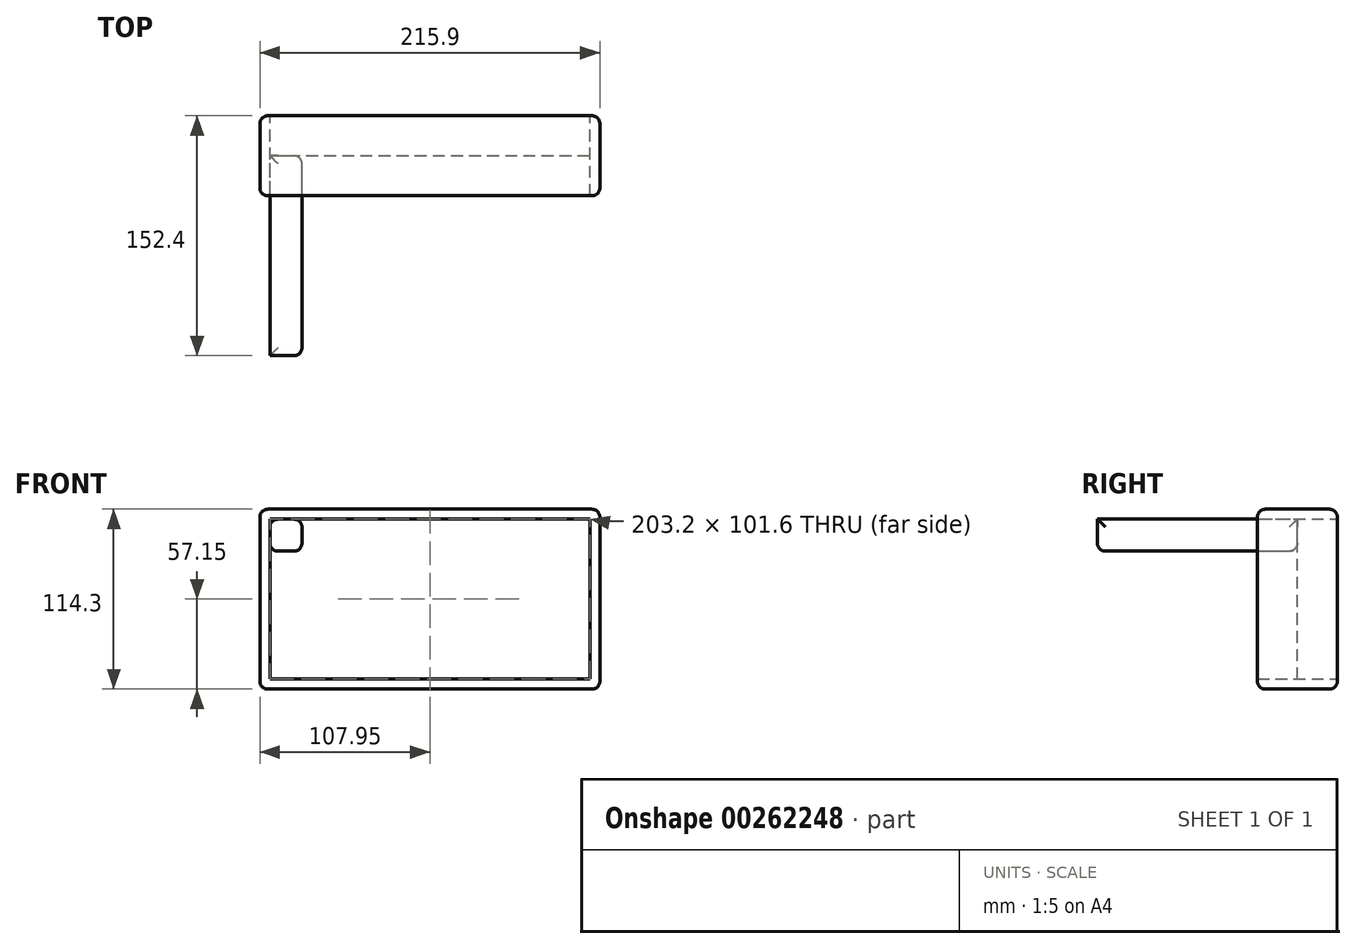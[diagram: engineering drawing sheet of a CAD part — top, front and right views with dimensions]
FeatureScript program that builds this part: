
annotation { "Feature Type Name" : "Feature", "Feature Type Description" : "" }
export const myFeature = defineFeature(function(context is Context, id is Id, definition is map)
    precondition{}
    {
        {
            var Q0;
            Q0=qCreatedBy(makeId("Front.planeOp"),FACE);
            var sketch = newSketch(context, id + "F0", { "sketchPlane" : qUnion([Q0])});
            skLineSegment(sketch, "E0.bottom", {"start": v(-101.6, -50.8) * mm, "end": v(101.6, -50.8) * mm});
            skLineSegment(sketch, "E0.top", {"start": v(-101.6, 50.8) * mm, "end": v(101.6, 50.8) * mm});
            skLineSegment(sketch, "E0.left", {"start": v(-101.6, -50.8) * mm, "end": v(-101.6, 50.8) * mm});
            skLineSegment(sketch, "E0.right", {"start": v(101.6, -50.8) * mm, "end": v(101.6, 50.8) * mm});
            skPoint(sketch, "E0.middle", {"position": v(0, 0) * mm});
            skLineSegment(sketch, "E1.bottom", {"start": v(-101.6, 30.48) * mm, "end": v(-81.28, 30.48) * mm});
            skLineSegment(sketch, "E1.top", {"start": v(-101.6, 50.8) * mm, "end": v(-81.28, 50.8) * mm});
            skLineSegment(sketch, "E1.left", {"start": v(-101.6, 30.48) * mm, "end": v(-101.6, 50.8) * mm});
            skLineSegment(sketch, "E1.right", {"start": v(-81.28, 30.48) * mm, "end": v(-81.28, 50.8) * mm});
            skLineSegment(sketch, "E2.bottom", {"start": v(101.6, 50.8) * mm, "end": v(81.28, 50.8) * mm});
            skLineSegment(sketch, "E2.top", {"start": v(101.6, 30.48) * mm, "end": v(81.28, 30.48) * mm});
            skLineSegment(sketch, "E2.left", {"start": v(101.6, 50.8) * mm, "end": v(101.6, 30.48) * mm});
            skLineSegment(sketch, "E2.right", {"start": v(81.28, 50.8) * mm, "end": v(81.28, 30.48) * mm});
            skLineSegment(sketch, "E3.bottom", {"start": v(101.6, -50.8) * mm, "end": v(81.28, -50.8) * mm});
            skLineSegment(sketch, "E3.top", {"start": v(101.6, -30.48) * mm, "end": v(81.28, -30.48) * mm});
            skLineSegment(sketch, "E3.left", {"start": v(101.6, -50.8) * mm, "end": v(101.6, -30.48) * mm});
            skLineSegment(sketch, "E3.right", {"start": v(81.28, -50.8) * mm, "end": v(81.28, -30.48) * mm});
            skLineSegment(sketch, "E4.bottom", {"start": v(-101.6, -50.8) * mm, "end": v(-81.28, -50.8) * mm});
            skLineSegment(sketch, "E4.top", {"start": v(-101.6, -30.48) * mm, "end": v(-81.28, -30.48) * mm});
            skLineSegment(sketch, "E4.left", {"start": v(-101.6, -50.8) * mm, "end": v(-101.6, -30.48) * mm});
            skLineSegment(sketch, "E4.right", {"start": v(-81.28, -50.8) * mm, "end": v(-81.28, -30.48) * mm});
            skLineSegment(sketch, "E5", {"start": v(-81.28, 30.48) * mm, "end": v(81.28, 30.48) * mm});
            skLineSegment(sketch, "E6", {"start": v(81.28, 30.48) * mm, "end": v(81.28, -30.48) * mm});
            skLineSegment(sketch, "E7", {"start": v(-81.28, 30.48) * mm, "end": v(-81.28, -30.48) * mm});
            skLineSegment(sketch, "E8", {"start": v(-81.28, -30.48) * mm, "end": v(81.28, -30.48) * mm});
            skLineSegment(sketch, "E9.bottom", {"start": v(107.95, -57.15) * mm, "end": v(-107.95, -57.15) * mm});
            skLineSegment(sketch, "E9.top", {"start": v(107.95, 57.15) * mm, "end": v(-107.95, 57.15) * mm});
            skLineSegment(sketch, "E9.left", {"start": v(107.95, -57.15) * mm, "end": v(107.95, 57.15) * mm});
            skLineSegment(sketch, "E9.right", {"start": v(-107.95, -57.15) * mm, "end": v(-107.95, 57.15) * mm});
            skLineSegment(sketch, "E10", {"start": v(0, 57.15) * mm, "end": v(0, -57.15) * mm});
            skSolve(sketch);
        }
        {
            var Q0;
            Q0=makeQuery(id+"F0.imprint","IMPRINT",FACE,{"disambiguationData":[TD([[makeQuery(id+"F0.imprint","IMPRINT",EDGE,{"derivedFrom":sQuery(id+"F0.wireOp",EDGE,"E0.right")}),-1.0]])]});
            var Q1;
            Q1=makeQuery(id+"F0.imprint","IMPRINT",FACE,{"disambiguationData":[TD([[makeQuery(id+"F0.imprint","IMPRINT",EDGE,{"derivedFrom":sQuery(id+"F0.wireOp",EDGE,"E0.left")}),1.0]])]});
            extrude(context, id + "F1", {"entities" : qUnion([Q0, Q1]), "endBound" : BoundingType.SYMMETRIC, "depth" : 50.8 * mm});
        }
        {
            var Q0;
            Q0=makeQuery(id+"F0.imprint","IMPRINT",FACE,{"disambiguationData":[TD([[makeQuery(id+"F0.imprint","IMPRINT",EDGE,{"derivedFrom":sQuery(id+"F0.wireOp",EDGE,"E1.bottom")}),1.0]])]});
            var Q1;
            Q1=makeQuery(id+"F0.imprint","IMPRINT",FACE,{"disambiguationData":[TD([[makeQuery(id+"F0.imprint","IMPRINT",EDGE,{"derivedFrom":sQuery(id+"F0.wireOp",EDGE,"E4.bottom")}),1.0]])]});
            var Q2;
            Q2=makeQuery(id+"F0.imprint","IMPRINT",FACE,{"disambiguationData":[TD([[makeQuery(id+"F0.imprint","IMPRINT",EDGE,{"derivedFrom":sQuery(id+"F0.wireOp",EDGE,"E3.bottom")}),-1.0]])]});
            var Q3;
            Q3=makeQuery(id+"F0.imprint","IMPRINT",FACE,{"disambiguationData":[TD([[makeQuery(id+"F0.imprint","IMPRINT",EDGE,{"derivedFrom":sQuery(id+"F0.wireOp",EDGE,"E2.bottom")}),1.0]])]});
            extrude(context, id + "F2", {"entities" : qUnion([Q0, Q1, Q2, Q3]), "depth" : 127 * mm});
        }
        {
            var Q0;
            Q0=makeQuery(id+"F0.imprint","IMPRINT",FACE,{"disambiguationData":[TD([[makeQuery(id+"F0.imprint","IMPRINT",EDGE,{"derivedFrom":sQuery(id+"F0.wireOp",EDGE,"E0.left")}),-1.0]])]});
            var Q1;
            {var subQ0=sQuery(id+"F0.wireOp",EDGE,"E1.right");Q1=makeQuery(id+"F0.imprint","IMPRINT",FACE,{"disambiguationData":[TD([[makeQuery(id+"F0.imprint","IMPRINT",EDGE,{"derivedFrom":subQ0}),-1.0]])]});}
            var Q2;
            {var subQ0=sQuery(id+"F0.wireOp",EDGE,"E2.right");Q2=makeQuery(id+"F0.imprint","IMPRINT",FACE,{"disambiguationData":[TD([[makeQuery(id+"F0.imprint","IMPRINT",EDGE,{"derivedFrom":subQ0}),-1.0]])]});}
            var Q3;
            Q3=makeQuery(id+"F0.imprint","IMPRINT",FACE,{"disambiguationData":[TD([[makeQuery(id+"F0.imprint","IMPRINT",EDGE,{"derivedFrom":sQuery(id+"F0.wireOp",EDGE,"E0.right")}),1.0]])]});
            var Q4;
            {var subQ0=sQuery(id+"F0.wireOp",EDGE,"E3.right");Q4=makeQuery(id+"F0.imprint","IMPRINT",FACE,{"disambiguationData":[TD([[makeQuery(id+"F0.imprint","IMPRINT",EDGE,{"derivedFrom":subQ0}),1.0]])]});}
            var Q5;
            {var subQ0=sQuery(id+"F0.wireOp",EDGE,"E4.right");Q5=makeQuery(id+"F0.imprint","IMPRINT",FACE,{"disambiguationData":[TD([[makeQuery(id+"F0.imprint","IMPRINT",EDGE,{"derivedFrom":subQ0}),-1.0]])]});}
            var Q6;
            {var subQ0=sQuery(id+"F0.wireOp",EDGE,"E6");Q6=makeQuery(id+"F0.imprint","IMPRINT",FACE,{"disambiguationData":[TD([[makeQuery(id+"F0.imprint","IMPRINT",EDGE,{"derivedFrom":subQ0}),-1.0]])]});}
            var Q7;
            {var subQ0=sQuery(id+"F0.wireOp",EDGE,"E7");Q7=makeQuery(id+"F0.imprint","IMPRINT",FACE,{"disambiguationData":[TD([[makeQuery(id+"F0.imprint","IMPRINT",EDGE,{"derivedFrom":subQ0}),1.0]])]});}
            var Q8;
            Q8=makeQuery(id+"F0.imprint","IMPRINT",FACE,{"disambiguationData":[TD([[makeQuery(id+"F0.imprint","IMPRINT",EDGE,{"derivedFrom":sQuery(id+"F0.wireOp",EDGE,"E1.bottom")}),1.0]])]});
            var Q9;
            Q9=makeQuery(id+"F0.imprint","IMPRINT",FACE,{"disambiguationData":[TD([[makeQuery(id+"F0.imprint","IMPRINT",EDGE,{"derivedFrom":sQuery(id+"F0.wireOp",EDGE,"E4.bottom")}),1.0]])]});
            var Q10;
            Q10=makeQuery(id+"F0.imprint","IMPRINT",FACE,{"disambiguationData":[TD([[makeQuery(id+"F0.imprint","IMPRINT",EDGE,{"derivedFrom":sQuery(id+"F0.wireOp",EDGE,"E2.bottom")}),1.0]])]});
            var Q11;
            Q11=makeQuery(id+"F0.imprint","IMPRINT",FACE,{"disambiguationData":[TD([[makeQuery(id+"F0.imprint","IMPRINT",EDGE,{"derivedFrom":sQuery(id+"F0.wireOp",EDGE,"E3.bottom")}),-1.0]])]});
            extrude(context, id + "F3", {"entities" : qUnion([Q0, Q1, Q2, Q3, Q4, Q5, Q6, Q7, Q8, Q9, Q10, Q11]), "depth" : 25.4 * mm});
        }
        {
            var Q0;
            Q0=makeQuery(id+"F1.opExtrude","CAP_EDGE",EDGE,{"disambiguationData":[OSD([sQuery(id+"F0.wireOp",EDGE,"E9.left")])],"isStart":true});
            var Q1;
            Q1=makeQuery(id+"F1.opExtrude","CAP_EDGE",EDGE,{"disambiguationData":[OSD([sQuery(id+"F0.wireOp",EDGE,"E9.bottom")])],"isStart":true});
            var Q2;
            Q2=makeQuery(id+"F1.opExtrude","CAP_EDGE",EDGE,{"disambiguationData":[OSD([sQuery(id+"F0.wireOp",EDGE,"E9.top")])],"isStart":true});
            var Q3;
            Q3=makeQuery(id+"F1.opExtrude","CAP_EDGE",EDGE,{"disambiguationData":[OSD([sQuery(id+"F0.wireOp",EDGE,"E9.right")])],"isStart":true});
            var Q4;
            Q4=makeQuery(id+"F1.opExtrude","CAP_EDGE",EDGE,{"disambiguationData":[OSD([sQuery(id+"F0.wireOp",EDGE,"E9.bottom")])],"isStart":false});
            var Q5;
            Q5=makeQuery(id+"F1.opExtrude","CAP_EDGE",EDGE,{"disambiguationData":[OSD([sQuery(id+"F0.wireOp",EDGE,"E9.right")])],"isStart":false});
            var Q6;
            Q6=makeQuery(id+"F1.opExtrude","CAP_EDGE",EDGE,{"disambiguationData":[OSD([sQuery(id+"F0.wireOp",EDGE,"E9.top")])],"isStart":false});
            var Q7;
            Q7=makeQuery(id+"F1.opExtrude","CAP_EDGE",EDGE,{"disambiguationData":[OSD([sQuery(id+"F0.wireOp",EDGE,"E9.left")])],"isStart":false});
            var Q8;
            Q8=makeQuery(id+"F1.opExtrude","SWEPT_EDGE",EDGE,{"disambiguationData":[OSD([sQuery(id+"F0.wireOp",EDGE,"E9.top"),sQuery(id+"F0.wireOp",EDGE,"E9.left")])]});
            var Q9;
            Q9=makeQuery(id+"F1.opExtrude","SWEPT_EDGE",EDGE,{"disambiguationData":[OSD([sQuery(id+"F0.wireOp",EDGE,"E9.bottom"),sQuery(id+"F0.wireOp",EDGE,"E9.left")])]});
            var Q10;
            Q10=makeQuery(id+"F1.opExtrude","SWEPT_EDGE",EDGE,{"disambiguationData":[OSD([sQuery(id+"F0.wireOp",EDGE,"E9.top"),sQuery(id+"F0.wireOp",EDGE,"E9.right")])]});
            var Q11;
            Q11=makeQuery(id+"F1.opExtrude","SWEPT_EDGE",EDGE,{"disambiguationData":[OSD([sQuery(id+"F0.wireOp",EDGE,"E9.bottom"),sQuery(id+"F0.wireOp",EDGE,"E9.right")])]});
            fillet(context, id + "F4", {"entities" : qUnion([Q0, Q1, Q2, Q3, Q4, Q5, Q6, Q7, Q8, Q9, Q10, Q11]), "radius" : 5.08 * mm, "tangentPropagation" : true, "allowEdgeOverflow" : false});
        }
        {
            var Q0;
            Q0=makeQuery(id+"F2.opExtrude","SWEPT_EDGE",EDGE,{"disambiguationData":[OSD([sQuery(id+"F0.wireOp",EDGE,"E0.bottom"),sQuery(id+"F0.wireOp",EDGE,"E4.bottom"),sQuery(id+"F0.wireOp",EDGE,"E4.right")])]});
            var Q1;
            Q1=makeQuery(id+"F2.opExtrude","SWEPT_EDGE",EDGE,{"disambiguationData":[OSD([sQuery(id+"F0.wireOp",EDGE,"E4.top"),sQuery(id+"F0.wireOp",EDGE,"E4.right"),sQuery(id+"F0.wireOp",EDGE,"E7"),sQuery(id+"F0.wireOp",EDGE,"E8")])]});
            var Q2;
            Q2=makeQuery(id+"F2.opExtrude","SWEPT_EDGE",EDGE,{"disambiguationData":[OSD([sQuery(id+"F0.wireOp",EDGE,"E4.bottom"),sQuery(id+"F0.wireOp",EDGE,"E4.left")])]});
            var Q3;
            Q3=makeQuery(id+"F2.opExtrude","SWEPT_EDGE",EDGE,{"disambiguationData":[OSD([sQuery(id+"F0.wireOp",EDGE,"E0.left"),sQuery(id+"F0.wireOp",EDGE,"E4.top"),sQuery(id+"F0.wireOp",EDGE,"E4.left")])]});
            var Q4;
            Q4=makeQuery(id+"F2.opExtrude","CAP_EDGE",EDGE,{"disambiguationData":[OSD([sQuery(id+"F0.wireOp",EDGE,"E4.bottom")])],"isStart":true});
            var Q5;
            Q5=makeQuery(id+"F2.opExtrude","CAP_EDGE",EDGE,{"disambiguationData":[OSD([sQuery(id+"F0.wireOp",EDGE,"E4.left")])],"isStart":true});
            var Q6;
            Q6=makeQuery(id+"F2.opExtrude","CAP_EDGE",EDGE,{"disambiguationData":[OSD([sQuery(id+"F0.wireOp",EDGE,"E4.top")])],"isStart":true});
            var Q7;
            Q7=makeQuery(id+"F2.opExtrude","CAP_EDGE",EDGE,{"disambiguationData":[OSD([sQuery(id+"F0.wireOp",EDGE,"E4.right")])],"isStart":false});
            var Q8;
            Q8=makeQuery(id+"F2.opExtrude","CAP_EDGE",EDGE,{"disambiguationData":[OSD([sQuery(id+"F0.wireOp",EDGE,"E4.bottom")])],"isStart":false});
            var Q9;
            Q9=makeQuery(id+"F2.opExtrude","CAP_EDGE",EDGE,{"disambiguationData":[OSD([sQuery(id+"F0.wireOp",EDGE,"E4.top")])],"isStart":false});
            var Q10;
            Q10=makeQuery(id+"F2.opExtrude","CAP_EDGE",EDGE,{"disambiguationData":[OSD([sQuery(id+"F0.wireOp",EDGE,"E4.left")])],"isStart":false});
            var Q11;
            Q11=makeQuery(id+"F2.opExtrude","CAP_EDGE",EDGE,{"disambiguationData":[OSD([sQuery(id+"F0.wireOp",EDGE,"E4.right")])],"isStart":true});
            var Q12;
            Q12=makeQuery(id+"F2.opExtrude","SWEPT_EDGE",EDGE,{"disambiguationData":[OSD([sQuery(id+"F0.wireOp",EDGE,"E0.top"),sQuery(id+"F0.wireOp",EDGE,"E1.top"),sQuery(id+"F0.wireOp",EDGE,"E1.right")])]});
            var Q13;
            Q13=makeQuery(id+"F2.opExtrude","SWEPT_EDGE",EDGE,{"disambiguationData":[OSD([sQuery(id+"F0.wireOp",EDGE,"E0.left"),sQuery(id+"F0.wireOp",EDGE,"E1.bottom"),sQuery(id+"F0.wireOp",EDGE,"E1.left")])]});
            var Q14;
            Q14=makeQuery(id+"F2.opExtrude","CAP_EDGE",EDGE,{"disambiguationData":[OSD([sQuery(id+"F0.wireOp",EDGE,"E1.bottom")])],"isStart":true});
            var Q15;
            Q15=makeQuery(id+"F2.opExtrude","SWEPT_EDGE",EDGE,{"disambiguationData":[OSD([sQuery(id+"F0.wireOp",EDGE,"E1.bottom"),sQuery(id+"F0.wireOp",EDGE,"E1.right"),sQuery(id+"F0.wireOp",EDGE,"E5"),sQuery(id+"F0.wireOp",EDGE,"E7")])]});
            var Q16;
            Q16=makeQuery(id+"F2.opExtrude","CAP_EDGE",EDGE,{"disambiguationData":[OSD([sQuery(id+"F0.wireOp",EDGE,"E1.right")])],"isStart":true});
            var Q17;
            Q17=makeQuery(id+"F2.opExtrude","CAP_EDGE",EDGE,{"disambiguationData":[OSD([sQuery(id+"F0.wireOp",EDGE,"E1.top")])],"isStart":true});
            var Q18;
            Q18=makeQuery(id+"F2.opExtrude","SWEPT_EDGE",EDGE,{"disambiguationData":[OSD([sQuery(id+"F0.wireOp",EDGE,"E1.top"),sQuery(id+"F0.wireOp",EDGE,"E1.left")])]});
            var Q19;
            Q19=makeQuery(id+"F2.opExtrude","CAP_EDGE",EDGE,{"disambiguationData":[OSD([sQuery(id+"F0.wireOp",EDGE,"E1.left")])],"isStart":true});
            var Q20;
            Q20=makeQuery(id+"F2.opExtrude","CAP_EDGE",EDGE,{"disambiguationData":[OSD([sQuery(id+"F0.wireOp",EDGE,"E1.right")])],"isStart":false});
            var Q21;
            Q21=makeQuery(id+"F2.opExtrude","CAP_EDGE",EDGE,{"disambiguationData":[OSD([sQuery(id+"F0.wireOp",EDGE,"E1.bottom")])],"isStart":false});
            var Q22;
            Q22=makeQuery(id+"F2.opExtrude","CAP_EDGE",EDGE,{"disambiguationData":[OSD([sQuery(id+"F0.wireOp",EDGE,"E1.top")])],"isStart":false});
            var Q23;
            Q23=makeQuery(id+"F2.opExtrude","CAP_EDGE",EDGE,{"disambiguationData":[OSD([sQuery(id+"F0.wireOp",EDGE,"E1.left")])],"isStart":false});
            var Q24;
            Q24=makeQuery(id+"F2.opExtrude","SWEPT_EDGE",EDGE,{"disambiguationData":[OSD([sQuery(id+"F0.wireOp",EDGE,"E2.top"),sQuery(id+"F0.wireOp",EDGE,"E2.right"),sQuery(id+"F0.wireOp",EDGE,"E5"),sQuery(id+"F0.wireOp",EDGE,"E6")])]});
            var Q25;
            Q25=makeQuery(id+"F2.opExtrude","SWEPT_EDGE",EDGE,{"disambiguationData":[OSD([sQuery(id+"F0.wireOp",EDGE,"E0.right"),sQuery(id+"F0.wireOp",EDGE,"E2.top"),sQuery(id+"F0.wireOp",EDGE,"E2.left")])]});
            var Q26;
            Q26=makeQuery(id+"F2.opExtrude","CAP_EDGE",EDGE,{"disambiguationData":[OSD([sQuery(id+"F0.wireOp",EDGE,"E2.bottom")])],"isStart":false});
            var Q27;
            Q27=makeQuery(id+"F2.opExtrude","SWEPT_EDGE",EDGE,{"disambiguationData":[OSD([sQuery(id+"F0.wireOp",EDGE,"E2.bottom"),sQuery(id+"F0.wireOp",EDGE,"E2.left")])]});
            var Q28;
            Q28=makeQuery(id+"F2.opExtrude","CAP_EDGE",EDGE,{"disambiguationData":[OSD([sQuery(id+"F0.wireOp",EDGE,"E2.right")])],"isStart":false});
            var Q29;
            Q29=makeQuery(id+"F2.opExtrude","CAP_EDGE",EDGE,{"disambiguationData":[OSD([sQuery(id+"F0.wireOp",EDGE,"E2.top")])],"isStart":false});
            var Q30;
            Q30=makeQuery(id+"F2.opExtrude","SWEPT_EDGE",EDGE,{"disambiguationData":[OSD([sQuery(id+"F0.wireOp",EDGE,"E0.top"),sQuery(id+"F0.wireOp",EDGE,"E2.bottom"),sQuery(id+"F0.wireOp",EDGE,"E2.right")])]});
            var Q31;
            Q31=makeQuery(id+"F2.opExtrude","CAP_EDGE",EDGE,{"disambiguationData":[OSD([sQuery(id+"F0.wireOp",EDGE,"E2.left")])],"isStart":false});
            var Q32;
            Q32=makeQuery(id+"F2.opExtrude","CAP_EDGE",EDGE,{"disambiguationData":[OSD([sQuery(id+"F0.wireOp",EDGE,"E2.left")])],"isStart":true});
            var Q33;
            Q33=makeQuery(id+"F2.opExtrude","CAP_EDGE",EDGE,{"disambiguationData":[OSD([sQuery(id+"F0.wireOp",EDGE,"E2.top")])],"isStart":true});
            var Q34;
            Q34=makeQuery(id+"F2.opExtrude","CAP_EDGE",EDGE,{"disambiguationData":[OSD([sQuery(id+"F0.wireOp",EDGE,"E3.bottom")])],"isStart":true});
            var Q35;
            Q35=makeQuery(id+"F2.opExtrude","SWEPT_EDGE",EDGE,{"disambiguationData":[OSD([sQuery(id+"F0.wireOp",EDGE,"E3.top"),sQuery(id+"F0.wireOp",EDGE,"E3.right"),sQuery(id+"F0.wireOp",EDGE,"E6"),sQuery(id+"F0.wireOp",EDGE,"E8")])]});
            var Q36;
            Q36=makeQuery(id+"F2.opExtrude","CAP_EDGE",EDGE,{"disambiguationData":[OSD([sQuery(id+"F0.wireOp",EDGE,"E3.top")])],"isStart":false});
            var Q37;
            Q37=makeQuery(id+"F2.opExtrude","SWEPT_EDGE",EDGE,{"disambiguationData":[OSD([sQuery(id+"F0.wireOp",EDGE,"E0.right"),sQuery(id+"F0.wireOp",EDGE,"E3.top"),sQuery(id+"F0.wireOp",EDGE,"E3.left")])]});
            var Q38;
            Q38=makeQuery(id+"F2.opExtrude","SWEPT_EDGE",EDGE,{"disambiguationData":[OSD([sQuery(id+"F0.wireOp",EDGE,"E3.bottom"),sQuery(id+"F0.wireOp",EDGE,"E3.left")])]});
            var Q39;
            Q39=makeQuery(id+"F2.opExtrude","CAP_EDGE",EDGE,{"disambiguationData":[OSD([sQuery(id+"F0.wireOp",EDGE,"E3.top")])],"isStart":true});
            var Q40;
            Q40=makeQuery(id+"F2.opExtrude","CAP_EDGE",EDGE,{"disambiguationData":[OSD([sQuery(id+"F0.wireOp",EDGE,"E3.left")])],"isStart":true});
            var Q41;
            Q41=makeQuery(id+"F2.opExtrude","CAP_EDGE",EDGE,{"disambiguationData":[OSD([sQuery(id+"F0.wireOp",EDGE,"E3.right")])],"isStart":true});
            var Q42;
            Q42=makeQuery(id+"F2.opExtrude","CAP_EDGE",EDGE,{"disambiguationData":[OSD([sQuery(id+"F0.wireOp",EDGE,"E3.left")])],"isStart":false});
            var Q43;
            Q43=makeQuery(id+"F2.opExtrude","CAP_EDGE",EDGE,{"disambiguationData":[OSD([sQuery(id+"F0.wireOp",EDGE,"E3.bottom")])],"isStart":false});
            var Q44;
            Q44=makeQuery(id+"F2.opExtrude","SWEPT_EDGE",EDGE,{"disambiguationData":[OSD([sQuery(id+"F0.wireOp",EDGE,"E0.bottom"),sQuery(id+"F0.wireOp",EDGE,"E3.bottom"),sQuery(id+"F0.wireOp",EDGE,"E3.right")])]});
            var Q45;
            Q45=makeQuery(id+"F2.opExtrude","CAP_EDGE",EDGE,{"disambiguationData":[OSD([sQuery(id+"F0.wireOp",EDGE,"E3.right")])],"isStart":false});
            fillet(context, id + "F5", {"entities" : qUnion([Q0, Q1, Q2, Q3, Q4, Q5, Q6, Q7, Q8, Q9, Q10, Q11, Q12, Q13, Q14, Q15, Q16, Q17, Q18, Q19, Q20, Q21, Q22, Q23, Q24, Q25, Q26, Q27, Q28, Q29, Q30, Q31, Q32, Q33, Q34, Q35, Q36, Q37, Q38, Q39, Q40, Q41, Q42, Q43, Q44, Q45]), "radius" : 5.08 * mm, "tangentPropagation" : true, "allowEdgeOverflow" : false});
        }
    });
